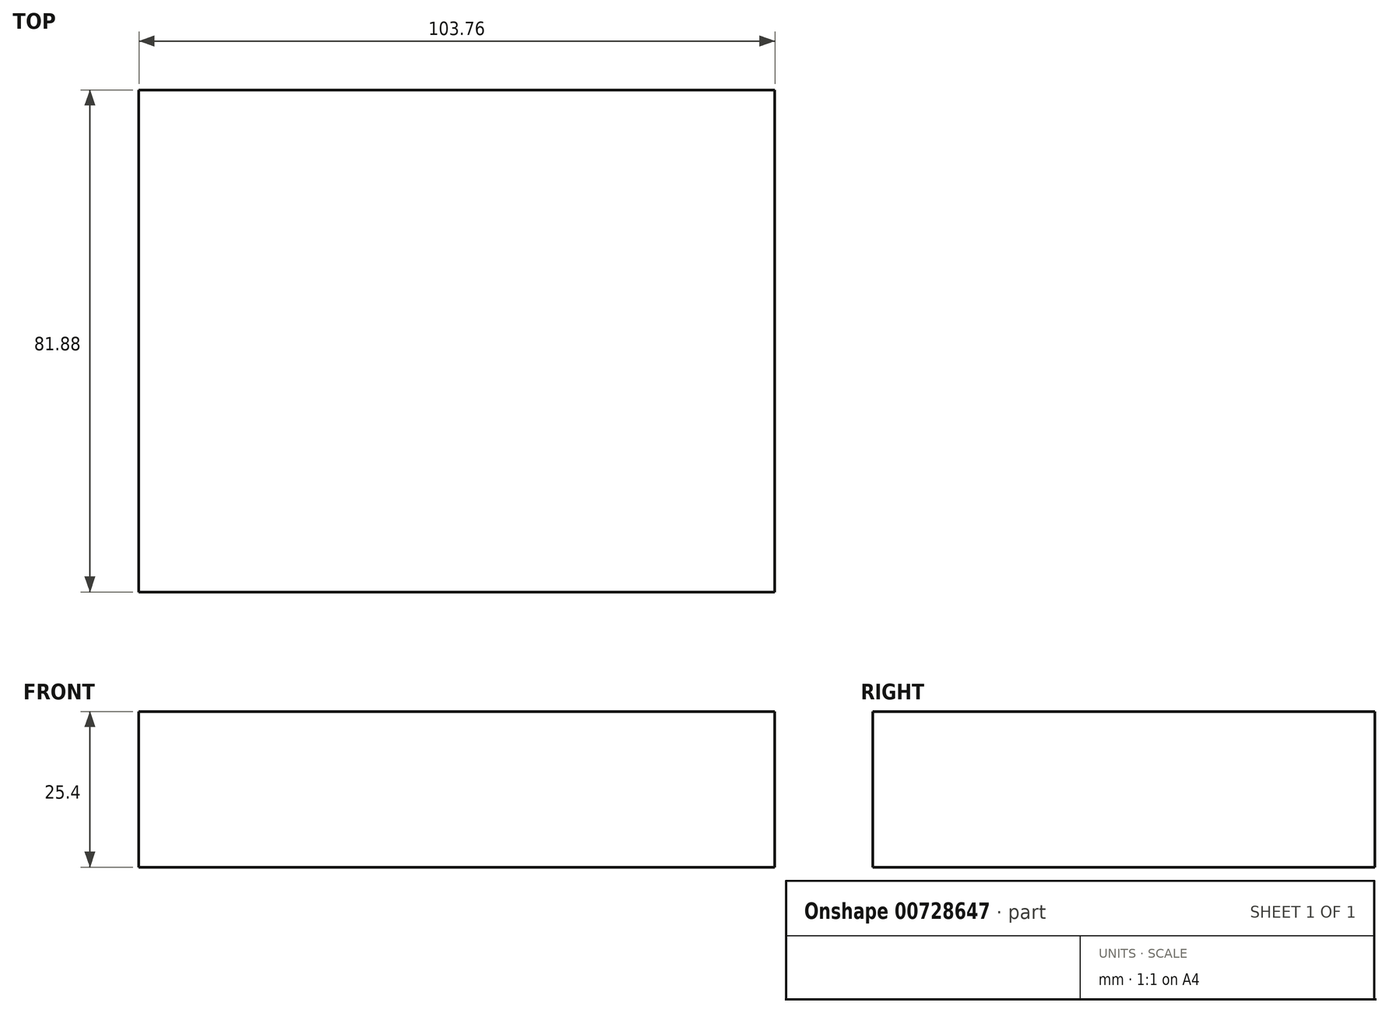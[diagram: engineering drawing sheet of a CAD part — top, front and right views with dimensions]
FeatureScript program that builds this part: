
annotation { "Feature Type Name" : "Feature", "Feature Type Description" : "" }
export const myFeature = defineFeature(function(context is Context, id is Id, definition is map)
    precondition{}
    {
        {
            var Q0;
            Q0=qCreatedBy(makeId("Top.planeOp"),FACE);
            var sketch = newSketch(context, id + "F0", { "sketchPlane" : qUnion([Q0])});
            skLineSegment(sketch, "E0.bottom", {"start": v(-48.56, 37.17) * mm, "end": v(55.2, 37.17) * mm});
            skLineSegment(sketch, "E0.top", {"start": v(-48.56, -44.71) * mm, "end": v(55.2, -44.71) * mm});
            skLineSegment(sketch, "E0.left", {"start": v(-48.56, 37.17) * mm, "end": v(-48.56, -44.71) * mm});
            skLineSegment(sketch, "E0.right", {"start": v(55.2, 37.17) * mm, "end": v(55.2, -44.71) * mm});
            skSolve(sketch);
        }
        {
            var Q0;
            Q0=makeQuery(id+"F0.imprint","IMPRINT",FACE,{"disambiguationData":[TD([[makeQuery(id+"F0.imprint","IMPRINT",EDGE,{"derivedFrom":sQuery(id+"F0.wireOp",EDGE,"E0.bottom")}),-1.0]])]});
            extrude(context, id + "F1", {"entities" : qUnion([Q0]), "depth" : 25.4 * mm, "offsetDistance" : 25.4 * mm});
        }
    });
